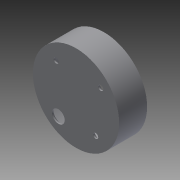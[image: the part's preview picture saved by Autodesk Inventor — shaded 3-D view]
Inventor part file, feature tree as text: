
AUTODESK INVENTOR PART (.ipt)
format: ipt  version: 2014 (Build 180170000, 170)  size: 193,536 bytes
history: native  units: mm
features: extrude x7, sketch x7, chamfer x5, projected_geometry x3
ambient origin geometry x8: Origin, YZ Plane, XZ Plane, XY Plane, X Axis, Y Axis, Z Axis, Center Point
bodies: Solid1 (feature_tree)
feature tree (22):
  extrude  "Extrusion1"  Depth=3.0mm TaperAngle=0.0deg
  extrude  "Extrusion2"  Depth=19.0mm TaperAngle=0.0deg
  extrude  "Extrusion3"  Depth=2.4mm
  chamfer  "Chamfer1"  Distance=16.5mm
  extrude  "Extrusion4"  Depth=10.0mm
  chamfer  "Chamfer2"  Distance=14.0mm
  extrude  "Extrusion5"  Depth=2.0mm TaperAngle=45.0deg
  extrude  "Extrusion6"  Depth=2.0mm
  chamfer  "Chamfer3"  Distance=40.0mm
  chamfer  "Chamfer4"  Distance=2.5mm
  extrude  "Extrusion7"  Depth=6.0mm
  chamfer  "Chamfer5"  Distance=2.5mm
  sketch  "Sketch1"  dims[d0=68.0mm d1=3.0mm d2=0.0mm]
  sketch  "Sketch2"  dims[d3=62.0mm d4=19.0mm d5=0.0mm]
  sketch  "Sketch3"  dims[d6=39.0mm d7=2.4mm]
  sketch  "Sketch4"  dims[d8=8.0mm]
  sketch  "Sketch5"  dims[d9=2.4mm]
  sketch  "Sketch6"  dims[d10=8.0mm d11=16.5mm d12=0.0mm]
  projected_geometry  "Projected Loop1"
  projected_geometry  "Projected Loop2"
  projected_geometry  "Projected Loop3"
  sketch  "Sketch7"  dims[d13=2.0mm d14=2.0mm d15=45.0deg d16=10.0mm d17=14.0mm d18=0.0mm d19=2.0mm d20=2.0mm d21=45.0deg d22=20.0mm d23=40.0mm d24=2.5mm d25=6.0mm d26=2.5mm d27=6.0mm d28=2.5mm d29=6.0mm d30=2.5mm d31=6.0mm d32=3.0mm d33=3.0mm d34=3.0mm d35=3.0mm d36=3.0mm d37=3.0mm d38=3.0mm d39=3.0mm d40=2.0mm d41=0.0mm d42=2.0mm d43=0.0mm d44=0.5mm d45=2.0mm d46=45.0deg d47=1.0mm d48=2.0mm d49=45.0deg d50=4.0mm d51=4.0mm d52=4.0mm d53=10.0mm d54=0.0mm d55=2.0mm d56=2.0mm d57=45.0deg]
